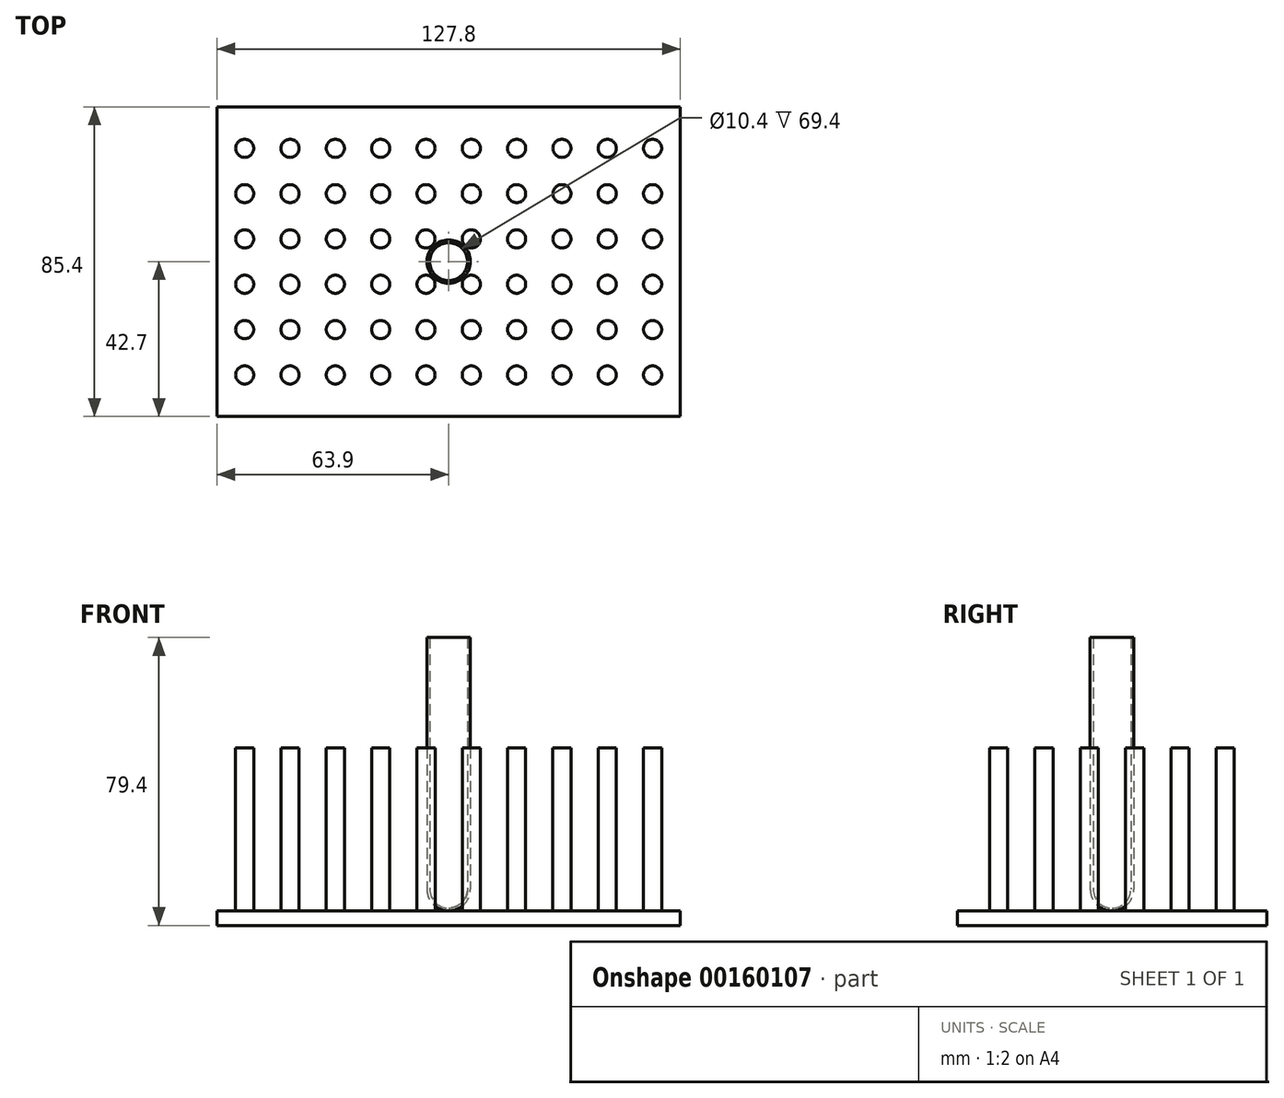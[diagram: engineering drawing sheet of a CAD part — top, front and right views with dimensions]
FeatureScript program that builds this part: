
annotation { "Feature Type Name" : "Feature", "Feature Type Description" : "" }
export const myFeature = defineFeature(function(context is Context, id is Id, definition is map)
    precondition{}
    {
        {
            var Q0;
            Q0=qCreatedBy(makeId("Front.planeOp"),FACE);
            var sketch = newSketch(context, id + "F0", { "sketchPlane" : qUnion([Q0])});
            skLineSegment(sketch, "E0", {"start": v(0, 0) * mm, "end": v(0, 0) * mm});
            skLineSegment(sketch, "E1", {"start": v(6, 6) * mm, "end": v(6, 75.4) * mm});
            skLineSegment(sketch, "E2", {"start": v(0, 0) * mm, "end": v(0, 71.65) * mm, "construction": true});
            skPoint(sketch, "E3.visualSharp", {"position": v(6, 0) * mm});
            skArc(sketch, "E3.filletArc", {"start": v(0, 0) * mm, "mid": v(4.24, 1.76) * mm, "end": v(6, 6) * mm});
            skLineSegment(sketch, "E4.0", {"start": v(5.2, 6) * mm, "end": v(5.2, 75.4) * mm});
            skArc(sketch, "E4.1", {"start": v(0, 0.8) * mm, "mid": v(3.68, 2.32) * mm, "end": v(5.2, 6) * mm});
            skLineSegment(sketch, "E5", {"start": v(0, 0.8) * mm, "end": v(0, 0) * mm});
            skLineSegment(sketch, "E6", {"start": v(6, 75.4) * mm, "end": v(5.2, 75.4) * mm});
            skSolve(sketch);
        }
        {
            var Q0;
            Q0 = qSketchRegion(id + "F0", true);
            var Q1;
            Q1=sQuery(id+"F0.wireOp",EDGE,"E2");
            revolve(context, id + "F1", {"entities" : qUnion([Q0]), "axis" : qUnion([Q1]), "revolveType" : RevolveType.FULL});
        }
        {
            var Q0;
            Q0=qCreatedBy(makeId("Top.planeOp"),FACE);
            var sketch = newSketch(context, id + "F2", { "sketchPlane" : qUnion([Q0])});
            skLineSegment(sketch, "E7.bottom", {"start": v(63.9, -42.7) * mm, "end": v(-63.9, -42.7) * mm});
            skLineSegment(sketch, "E7.top", {"start": v(63.9, 42.7) * mm, "end": v(-63.9, 42.7) * mm});
            skLineSegment(sketch, "E7.left", {"start": v(63.9, -42.7) * mm, "end": v(63.9, 42.7) * mm});
            skLineSegment(sketch, "E7.right", {"start": v(-63.9, -42.7) * mm, "end": v(-63.9, 42.7) * mm});
            skPoint(sketch, "E7.middle", {"position": v(0, 0) * mm});
            skSolve(sketch);
        }
        {
            var Q0;
            Q0 = qSketchRegion(id + "F2", true);
            extrude(context, id + "F3", {"entities" : qUnion([Q0]), "operationType" : NewBodyOperationType.ADD, "oppositeDirection" : true, "depth" : 4 * mm});
        }
        {
            var Q0;
            Q0=makeQuery(id+"F3.opExtrude","CAP_FACE",FACE,{"disambiguationData":[OSD([sQuery(id+"F2.wireOp",EDGE,"E7.bottom"),sQuery(id+"F2.wireOp",EDGE,"E7.top"),sQuery(id+"F2.wireOp",EDGE,"E7.left"),sQuery(id+"F2.wireOp",EDGE,"E7.right")])],"isStart":true});
            var sketch = newSketch(context, id + "F4", { "sketchPlane" : qUnion([Q0])});
            skCircle(sketch, "E8", {"center": v(-56.25, 31.25) * mm, "radius": 2.5 * mm});
            skCircle(sketch, "E9.0.1.0", {"center": v(-56.25, 18.75) * mm, "radius": 2.5 * mm});
            skCircle(sketch, "E9.0.2.0", {"center": v(-56.25, 6.25) * mm, "radius": 2.5 * mm});
            skCircle(sketch, "E9.0.3.0", {"center": v(-56.25, -6.25) * mm, "radius": 2.5 * mm});
            skCircle(sketch, "E9.0.4.0", {"center": v(-56.25, -18.75) * mm, "radius": 2.5 * mm});
            skCircle(sketch, "E9.0.5.0", {"center": v(-56.25, -31.25) * mm, "radius": 2.5 * mm});
            skCircle(sketch, "E9.1.0.0", {"center": v(-43.75, 31.25) * mm, "radius": 2.5 * mm});
            skCircle(sketch, "E9.1.1.0", {"center": v(-43.75, 18.75) * mm, "radius": 2.5 * mm});
            skCircle(sketch, "E9.1.2.0", {"center": v(-43.75, 6.25) * mm, "radius": 2.5 * mm});
            skCircle(sketch, "E9.1.3.0", {"center": v(-43.75, -6.25) * mm, "radius": 2.5 * mm});
            skCircle(sketch, "E9.1.4.0", {"center": v(-43.75, -18.75) * mm, "radius": 2.5 * mm});
            skCircle(sketch, "E9.1.5.0", {"center": v(-43.75, -31.25) * mm, "radius": 2.5 * mm});
            skCircle(sketch, "E9.2.0.0", {"center": v(-31.25, 31.25) * mm, "radius": 2.5 * mm});
            skCircle(sketch, "E9.2.1.0", {"center": v(-31.25, 18.75) * mm, "radius": 2.5 * mm});
            skCircle(sketch, "E9.2.2.0", {"center": v(-31.25, 6.25) * mm, "radius": 2.5 * mm});
            skCircle(sketch, "E9.2.3.0", {"center": v(-31.25, -6.25) * mm, "radius": 2.5 * mm});
            skCircle(sketch, "E9.2.4.0", {"center": v(-31.25, -18.75) * mm, "radius": 2.5 * mm});
            skCircle(sketch, "E9.2.5.0", {"center": v(-31.25, -31.25) * mm, "radius": 2.5 * mm});
            skCircle(sketch, "E9.3.0.0", {"center": v(-18.75, 31.25) * mm, "radius": 2.5 * mm});
            skCircle(sketch, "E9.3.1.0", {"center": v(-18.75, 18.75) * mm, "radius": 2.5 * mm});
            skCircle(sketch, "E9.3.2.0", {"center": v(-18.75, 6.25) * mm, "radius": 2.5 * mm});
            skCircle(sketch, "E9.3.3.0", {"center": v(-18.75, -6.25) * mm, "radius": 2.5 * mm});
            skCircle(sketch, "E9.3.4.0", {"center": v(-18.75, -18.75) * mm, "radius": 2.5 * mm});
            skCircle(sketch, "E9.3.5.0", {"center": v(-18.75, -31.25) * mm, "radius": 2.5 * mm});
            skCircle(sketch, "E9.4.0.0", {"center": v(-6.25, 31.25) * mm, "radius": 2.5 * mm});
            skCircle(sketch, "E9.4.1.0", {"center": v(-6.25, 18.75) * mm, "radius": 2.5 * mm});
            skCircle(sketch, "E9.4.2.0", {"center": v(-6.25, 6.25) * mm, "radius": 2.5 * mm});
            skCircle(sketch, "E9.4.3.0", {"center": v(-6.25, -6.25) * mm, "radius": 2.5 * mm});
            skCircle(sketch, "E9.4.4.0", {"center": v(-6.25, -18.75) * mm, "radius": 2.5 * mm});
            skCircle(sketch, "E9.4.5.0", {"center": v(-6.25, -31.25) * mm, "radius": 2.5 * mm});
            skCircle(sketch, "E9.5.0.0", {"center": v(6.25, 31.25) * mm, "radius": 2.5 * mm});
            skCircle(sketch, "E9.5.1.0", {"center": v(6.25, 18.75) * mm, "radius": 2.5 * mm});
            skCircle(sketch, "E9.5.2.0", {"center": v(6.25, 6.25) * mm, "radius": 2.5 * mm});
            skCircle(sketch, "E9.5.3.0", {"center": v(6.25, -6.25) * mm, "radius": 2.5 * mm});
            skCircle(sketch, "E9.5.4.0", {"center": v(6.25, -18.75) * mm, "radius": 2.5 * mm});
            skCircle(sketch, "E9.5.5.0", {"center": v(6.25, -31.25) * mm, "radius": 2.5 * mm});
            skCircle(sketch, "E9.6.0.0", {"center": v(18.75, 31.25) * mm, "radius": 2.5 * mm});
            skCircle(sketch, "E9.6.1.0", {"center": v(18.75, 18.75) * mm, "radius": 2.5 * mm});
            skCircle(sketch, "E9.6.2.0", {"center": v(18.75, 6.25) * mm, "radius": 2.5 * mm});
            skCircle(sketch, "E9.6.3.0", {"center": v(18.75, -6.25) * mm, "radius": 2.5 * mm});
            skCircle(sketch, "E9.6.4.0", {"center": v(18.75, -18.75) * mm, "radius": 2.5 * mm});
            skCircle(sketch, "E9.6.5.0", {"center": v(18.75, -31.25) * mm, "radius": 2.5 * mm});
            skCircle(sketch, "E9.7.0.0", {"center": v(31.25, 31.25) * mm, "radius": 2.5 * mm});
            skCircle(sketch, "E9.7.1.0", {"center": v(31.25, 18.75) * mm, "radius": 2.5 * mm});
            skCircle(sketch, "E9.7.2.0", {"center": v(31.25, 6.25) * mm, "radius": 2.5 * mm});
            skCircle(sketch, "E9.7.3.0", {"center": v(31.25, -6.25) * mm, "radius": 2.5 * mm});
            skCircle(sketch, "E9.7.4.0", {"center": v(31.25, -18.75) * mm, "radius": 2.5 * mm});
            skCircle(sketch, "E9.7.5.0", {"center": v(31.25, -31.25) * mm, "radius": 2.5 * mm});
            skCircle(sketch, "E9.8.0.0", {"center": v(43.75, 31.25) * mm, "radius": 2.5 * mm});
            skCircle(sketch, "E9.8.1.0", {"center": v(43.75, 18.75) * mm, "radius": 2.5 * mm});
            skCircle(sketch, "E9.8.2.0", {"center": v(43.75, 6.25) * mm, "radius": 2.5 * mm});
            skCircle(sketch, "E9.8.3.0", {"center": v(43.75, -6.25) * mm, "radius": 2.5 * mm});
            skCircle(sketch, "E9.8.4.0", {"center": v(43.75, -18.75) * mm, "radius": 2.5 * mm});
            skCircle(sketch, "E9.8.5.0", {"center": v(43.75, -31.25) * mm, "radius": 2.5 * mm});
            skCircle(sketch, "E9.9.0.0", {"center": v(56.25, 31.25) * mm, "radius": 2.5 * mm});
            skCircle(sketch, "E9.9.1.0", {"center": v(56.25, 18.75) * mm, "radius": 2.5 * mm});
            skCircle(sketch, "E9.9.2.0", {"center": v(56.25, 6.25) * mm, "radius": 2.5 * mm});
            skCircle(sketch, "E9.9.3.0", {"center": v(56.25, -6.25) * mm, "radius": 2.5 * mm});
            skCircle(sketch, "E9.9.4.0", {"center": v(56.25, -18.75) * mm, "radius": 2.5 * mm});
            skCircle(sketch, "E9.9.5.0", {"center": v(56.25, -31.25) * mm, "radius": 2.5 * mm});
            skLineSegment(sketch, "E9.direction1", {"start": v(-56.25, 31.25) * mm, "end": v(-43.75, 31.25) * mm, "construction": true});
            skLineSegment(sketch, "E9.direction2", {"start": v(-56.25, 31.25) * mm, "end": v(-56.25, 18.75) * mm, "construction": true});
            skLineSegment(sketch, "E10", {"start": v(-63.9, 0) * mm, "end": v(63.9, 0) * mm, "construction": true});
            skLineSegment(sketch, "E11", {"start": v(-56.25, 6.25) * mm, "end": v(-56.25, 0) * mm, "construction": true});
            skLineSegment(sketch, "E12", {"start": v(-56.25, 0) * mm, "end": v(-56.25, -6.25) * mm, "construction": true});
            skLineSegment(sketch, "E13", {"start": v(-56.25, -31.25) * mm, "end": v(-63.9, -31.25) * mm, "construction": true});
            skLineSegment(sketch, "E14", {"start": v(56.25, -31.25) * mm, "end": v(63.9, -31.25) * mm, "construction": true});
            skSolve(sketch);
        }
        {
            var Q0;
            Q0 = qSketchRegion(id + "F4", true);
            extrude(context, id + "F5", {"entities" : qUnion([Q0]), "operationType" : NewBodyOperationType.ADD, "depth" : 45 * mm});
        }
    });
